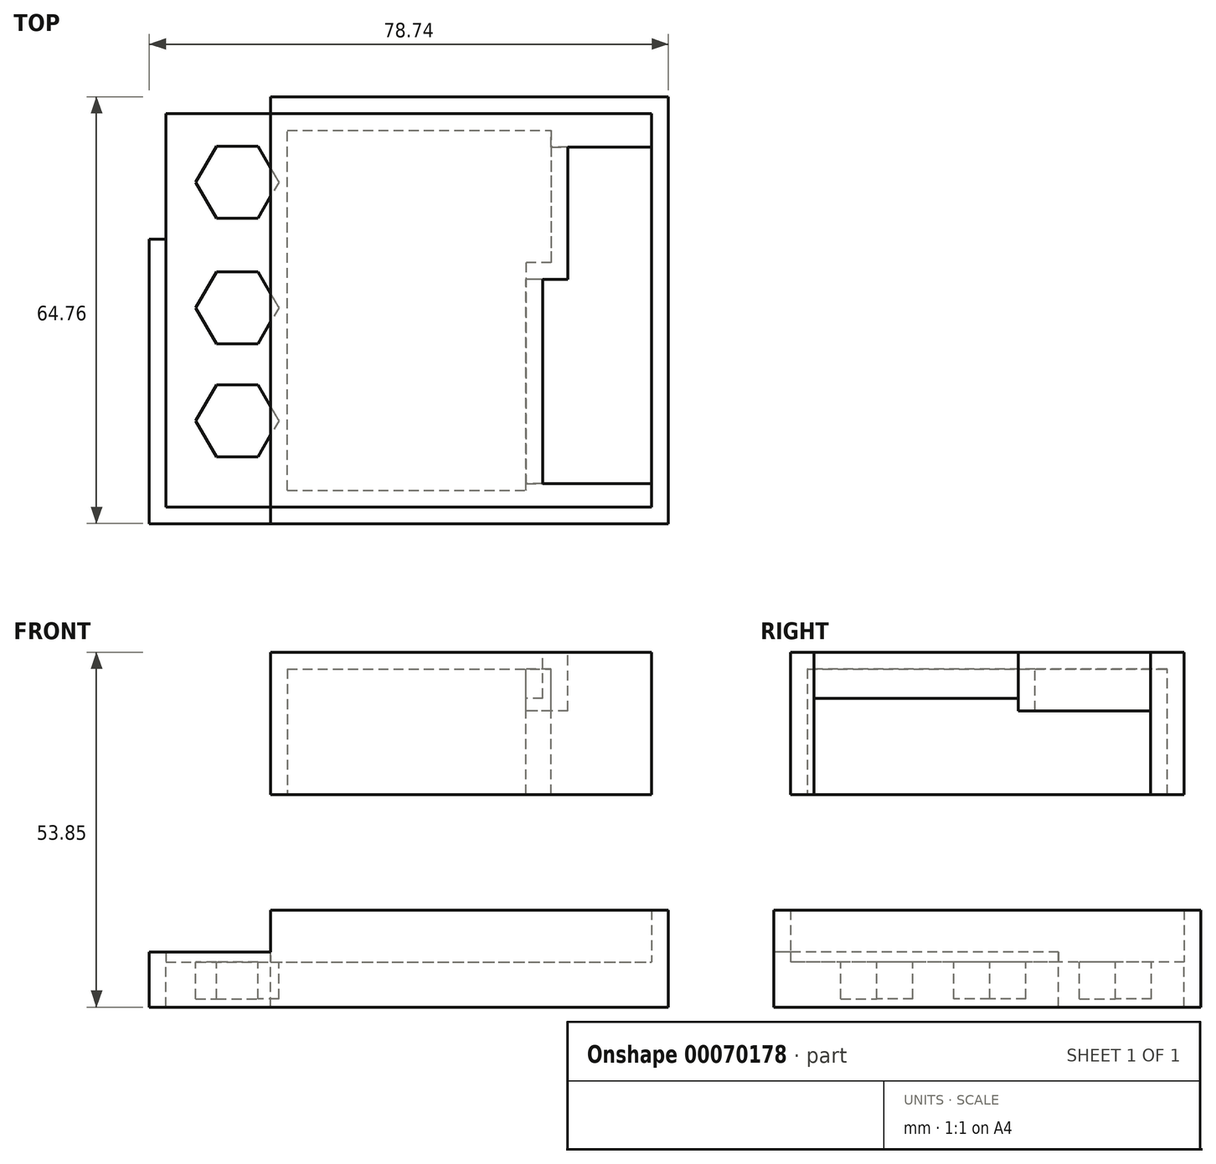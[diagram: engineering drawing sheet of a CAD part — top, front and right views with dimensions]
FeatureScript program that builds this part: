
annotation { "Feature Type Name" : "Feature", "Feature Type Description" : "" }
export const myFeature = defineFeature(function(context is Context, id is Id, definition is map)
    precondition{}
    {
        {
            var Q0;
            Q0=qCreatedBy(makeId("Top.planeOp"),FACE);
            var sketch = newSketch(context, id + "F0", { "sketchPlane" : qUnion([Q0])});
            skLineSegment(sketch, "E0.bottom", {"start": v(-35.56, 28.58) * mm, "end": v(35.56, 28.58) * mm, "construction": true});
            skLineSegment(sketch, "E0.top", {"start": v(-35.56, -28.58) * mm, "end": v(35.56, -28.58) * mm, "construction": true});
            skLineSegment(sketch, "E0.left", {"start": v(-35.56, 28.58) * mm, "end": v(-35.56, -28.58) * mm, "construction": true});
            skLineSegment(sketch, "E0.right", {"start": v(35.56, 28.58) * mm, "end": v(35.56, -28.58) * mm, "construction": true});
            skLineSegment(sketch, "E1", {"start": v(0, 28.58) * mm, "end": v(0, -28.58) * mm, "construction": true});
            skLineSegment(sketch, "E2.0", {"start": v(-36.83, 29.84) * mm, "end": v(36.83, 29.84) * mm});
            skLineSegment(sketch, "E2.1", {"start": v(-36.83, 29.84) * mm, "end": v(-36.83, -29.84) * mm});
            skLineSegment(sketch, "E2.2", {"start": v(-36.83, -29.84) * mm, "end": v(36.83, -29.84) * mm});
            skLineSegment(sketch, "E2.3", {"start": v(36.83, 29.84) * mm, "end": v(36.83, -29.84) * mm});
            skLineSegment(sketch, "E3.0", {"start": v(-39.37, 32.38) * mm, "end": v(39.37, 32.38) * mm});
            skLineSegment(sketch, "E3.1", {"start": v(-39.37, 32.39) * mm, "end": v(-39.37, -32.39) * mm});
            skLineSegment(sketch, "E3.2", {"start": v(-39.37, -32.38) * mm, "end": v(39.37, -32.38) * mm});
            skLineSegment(sketch, "E3.3", {"start": v(39.37, 32.39) * mm, "end": v(39.37, -32.38) * mm});
            skLineSegment(sketch, "E4.bottom", {"start": v(-20.96, 10.8) * mm, "end": v(-39.37, 10.8) * mm});
            skLineSegment(sketch, "E4.top", {"start": v(-20.96, 32.38) * mm, "end": v(-39.37, 32.38) * mm});
            skLineSegment(sketch, "E4.left", {"start": v(-20.96, 10.8) * mm, "end": v(-20.96, 32.38) * mm});
            skLineSegment(sketch, "E4.right", {"start": v(-39.37, 10.8) * mm, "end": v(-39.37, 32.38) * mm});
            skLineSegment(sketch, "E5.MirrorCS", {"start": v(-20.96, -10.8) * mm, "end": v(-39.37, -10.8) * mm});
            skLineSegment(sketch, "E6.MirrorCS", {"start": v(-20.96, -10.8) * mm, "end": v(-20.96, -32.38) * mm});
            skLineSegment(sketch, "E7", {"start": v(-20.96, -10.8) * mm, "end": v(-20.96, 10.8) * mm});
            skSolve(sketch);
        }
        {
            var Q0;
            {var subQ4=sQuery(id+"F0.wireOp",EDGE,"E4.top");Q0=makeQuery(id+"F0.imprint","IMPRINT",FACE,{"disambiguationData":[TD([[makeQuery(id+"F0.imprint","IMPRINT",EDGE,{"derivedFrom":subQ4}),1.0]])]});}
            var Q1;
            {var subQ0=sQuery(id+"F0.wireOp",EDGE,"E2.1");var subQ1=sQuery(id+"F0.wireOp",EDGE,"E2.0");var subQ2=makeQuery(id+"F0.imprint","INTERSECT",VERTEX,{"derivedFrom":[subQ1,subQ0]});Q1=makeQuery(id+"F0.imprint","IMPRINT",FACE,{"disambiguationData":[TD([[makeQuery(id+"F0.imprint","IMPRINT",EDGE,{"disambiguationData":[TD([[subQ2,-1.0]])],"derivedFrom":subQ1}),-1.0]])]});}
            var Q2;
            {var subQ0=sQuery(id+"F0.wireOp",EDGE,"E2.3");Q2=makeQuery(id+"F0.imprint","IMPRINT",FACE,{"disambiguationData":[TD([[makeQuery(id+"F0.imprint","IMPRINT",EDGE,{"derivedFrom":subQ0}),-1.0]])]});}
            var Q3;
            {var subQ7=sQuery(id+"F0.wireOp",EDGE,"E2.2");var subQ8=sQuery(id+"F0.wireOp",EDGE,"E2.1");var subQ9=makeQuery(id+"F0.imprint","INTERSECT",VERTEX,{"derivedFrom":[subQ8,subQ7]});Q3=makeQuery(id+"F0.imprint","IMPRINT",FACE,{"disambiguationData":[TD([[makeQuery(id+"F0.imprint","IMPRINT",EDGE,{"disambiguationData":[TD([[subQ9,1.0]])],"derivedFrom":subQ8}),-1.0]])]});}
            var Q4;
            {var subQ0=sQuery(id+"F0.wireOp",EDGE,"E4.bottom");var subQ1=sQuery(id+"F0.wireOp",EDGE,"E2.1");var subQ2=makeQuery(id+"F0.imprint","INTERSECT",VERTEX,{"derivedFrom":[subQ1,subQ0]});Q4=makeQuery(id+"F0.imprint","IMPRINT",FACE,{"disambiguationData":[TD([[makeQuery(id+"F0.imprint","IMPRINT",EDGE,{"disambiguationData":[TD([[subQ2,-1.0]])],"derivedFrom":subQ1}),-1.0]])]});}
            var Q5;
            {var subQ0=sQuery(id+"F0.wireOp",EDGE,"E2.2");var subQ1=sQuery(id+"F0.wireOp",EDGE,"E2.1");var subQ2=makeQuery(id+"F0.imprint","INTERSECT",VERTEX,{"derivedFrom":[subQ1,subQ0]});Q5=makeQuery(id+"F0.imprint","IMPRINT",FACE,{"disambiguationData":[TD([[makeQuery(id+"F0.imprint","IMPRINT",EDGE,{"disambiguationData":[TD([[subQ2,1.0]])],"derivedFrom":subQ1}),1.0]])]});}
            var Q6;
            {var subQ1=sQuery(id+"F0.wireOp",EDGE,"E2.3");Q6=makeQuery(id+"F0.imprint","IMPRINT",FACE,{"disambiguationData":[TD([[makeQuery(id+"F0.imprint","IMPRINT",EDGE,{"derivedFrom":subQ1}),1.0]])]});}
            var Q7;
            {var subQ5=sQuery(id+"F0.wireOp",EDGE,"E7");Q7=makeQuery(id+"F0.imprint","IMPRINT",FACE,{"disambiguationData":[TD([[makeQuery(id+"F0.imprint","IMPRINT",EDGE,{"derivedFrom":subQ5}),1.0]])]});}
            extrude(context, id + "F1", {"entities" : qUnion([Q0, Q1, Q2, Q3, Q4, Q5, Q6, Q7]), "oppositeDirection" : true, "depth" : 6.86 * mm});
        }
        {
            var Q0;
            {var subQ1=sQuery(id+"F0.wireOp",EDGE,"E2.3");Q0=makeQuery(id+"F0.imprint","IMPRINT",FACE,{"disambiguationData":[TD([[makeQuery(id+"F0.imprint","IMPRINT",EDGE,{"derivedFrom":subQ1}),1.0]])]});}
            var Q1;
            {var subQ7=sQuery(id+"F0.wireOp",EDGE,"E2.2");var subQ8=sQuery(id+"F0.wireOp",EDGE,"E2.1");var subQ9=makeQuery(id+"F0.imprint","INTERSECT",VERTEX,{"derivedFrom":[subQ8,subQ7]});Q1=makeQuery(id+"F0.imprint","IMPRINT",FACE,{"disambiguationData":[TD([[makeQuery(id+"F0.imprint","IMPRINT",EDGE,{"disambiguationData":[TD([[subQ9,1.0]])],"derivedFrom":subQ8}),-1.0]])]});}
            var Q2;
            {var subQ0=sQuery(id+"F0.wireOp",EDGE,"E4.bottom");var subQ1=sQuery(id+"F0.wireOp",EDGE,"E2.1");var subQ2=makeQuery(id+"F0.imprint","INTERSECT",VERTEX,{"derivedFrom":[subQ1,subQ0]});Q2=makeQuery(id+"F0.imprint","IMPRINT",FACE,{"disambiguationData":[TD([[makeQuery(id+"F0.imprint","IMPRINT",EDGE,{"disambiguationData":[TD([[subQ2,-1.0]])],"derivedFrom":subQ1}),-1.0]])]});}
            var Q3;
            {var subQ4=sQuery(id+"F0.wireOp",EDGE,"E4.top");Q3=makeQuery(id+"F0.imprint","IMPRINT",FACE,{"disambiguationData":[TD([[makeQuery(id+"F0.imprint","IMPRINT",EDGE,{"derivedFrom":subQ4}),1.0]])]});}
            extrude(context, id + "F2", {"entities" : qUnion([Q0, Q1, Q2, Q3]), "operationType" : NewBodyOperationType.ADD, "depth" : 1.52 * mm});
        }
        {
            var Q0;
            Q0=makeQuery(id+"F2.opExtrude","CAP_FACE",FACE,{"disambiguationData":[OSD([sQuery(id+"F0.wireOp",EDGE,"E2.0"),sQuery(id+"F0.wireOp",EDGE,"E2.1"),sQuery(id+"F0.wireOp",EDGE,"E2.2"),sQuery(id+"F0.wireOp",EDGE,"E2.3"),sQuery(id+"F0.wireOp",EDGE,"E3.0"),sQuery(id+"F0.wireOp",EDGE,"E3.1"),sQuery(id+"F0.wireOp",EDGE,"E3.2"),sQuery(id+"F0.wireOp",EDGE,"E3.3")])],"isStart":false});
            extrude(context, id + "F3", {"entities" : qUnion([Q0]), "operationType" : NewBodyOperationType.ADD, "depth" : 6.35 * mm});
        }
        {
            var Q0;
            {var subQ4=sQuery(id+"F0.wireOp",EDGE,"E4.top");Q0=makeQuery(id+"F0.imprint","IMPRINT",FACE,{"disambiguationData":[TD([[makeQuery(id+"F0.imprint","IMPRINT",EDGE,{"derivedFrom":subQ4}),1.0]])]});}
            var Q1;
            {var subQ0=sQuery(id+"F0.wireOp",EDGE,"E2.1");var subQ1=sQuery(id+"F0.wireOp",EDGE,"E2.0");var subQ2=makeQuery(id+"F0.imprint","INTERSECT",VERTEX,{"derivedFrom":[subQ1,subQ0]});Q1=makeQuery(id+"F0.imprint","IMPRINT",FACE,{"disambiguationData":[TD([[makeQuery(id+"F0.imprint","IMPRINT",EDGE,{"disambiguationData":[TD([[subQ2,-1.0]])],"derivedFrom":subQ1}),-1.0]])]});}
            var Q2;
            {var subQ0=sQuery(id+"F0.wireOp",EDGE,"E2.2");var subQ1=sQuery(id+"F0.wireOp",EDGE,"E2.1");var subQ2=makeQuery(id+"F0.imprint","INTERSECT",VERTEX,{"derivedFrom":[subQ1,subQ0]});Q2=makeQuery(id+"F0.imprint","IMPRINT",FACE,{"disambiguationData":[TD([[makeQuery(id+"F0.imprint","IMPRINT",EDGE,{"disambiguationData":[TD([[subQ2,1.0]])],"derivedFrom":subQ1}),1.0]])]});}
            var Q3;
            {var subQ7=sQuery(id+"F0.wireOp",EDGE,"E2.2");var subQ8=sQuery(id+"F0.wireOp",EDGE,"E2.1");var subQ9=makeQuery(id+"F0.imprint","INTERSECT",VERTEX,{"derivedFrom":[subQ8,subQ7]});Q3=makeQuery(id+"F0.imprint","IMPRINT",FACE,{"disambiguationData":[TD([[makeQuery(id+"F0.imprint","IMPRINT",EDGE,{"disambiguationData":[TD([[subQ9,1.0]])],"derivedFrom":subQ8}),-1.0]])]});}
            var Q4;
            {var subQ0=sQuery(id+"F0.wireOp",EDGE,"E4.bottom");var subQ1=sQuery(id+"F0.wireOp",EDGE,"E2.1");var subQ2=makeQuery(id+"F0.imprint","INTERSECT",VERTEX,{"derivedFrom":[subQ1,subQ0]});Q4=makeQuery(id+"F0.imprint","IMPRINT",FACE,{"disambiguationData":[TD([[makeQuery(id+"F0.imprint","IMPRINT",EDGE,{"disambiguationData":[TD([[subQ2,-1.0]])],"derivedFrom":subQ1}),-1.0]])]});}
            extrude(context, id + "F4", {"entities" : qUnion([Q0, Q1, Q2, Q3, Q4]), "operationType" : NewBodyOperationType.REMOVE, "depth" : 25.4 * mm, "hasSecondDirection" : true, "secondDirectionOppositeDirection" : false, "secondDirectionDepth" : 1.52 * mm});
        }
        {
            var Q0;
            {var subQ0=sQuery(id+"F0.wireOp",EDGE,"E2.3");Q0=makeQuery(id+"F0.imprint","IMPRINT",FACE,{"disambiguationData":[TD([[makeQuery(id+"F0.imprint","IMPRINT",EDGE,{"derivedFrom":subQ0}),-1.0]])]});}
            extrude(context, id + "F5", {"entities" : qUnion([Q0]), "operationType" : NewBodyOperationType.ADD, "depth" : 47 * mm, "hasSecondDirection" : true, "secondDirectionOppositeDirection" : false, "secondDirectionDepth" : 25.4 * mm});
        }
        {
            var Q0;
            Q0=makeQuery(id+"F5.opExtrude","CAP_FACE",FACE,{"disambiguationData":[OSD([sQuery(id+"F0.wireOp",EDGE,"E2.0"),sQuery(id+"F0.wireOp",EDGE,"E2.2"),sQuery(id+"F0.wireOp",EDGE,"E2.3"),sQuery(id+"F0.wireOp",EDGE,"E4.left"),sQuery(id+"F0.wireOp",EDGE,"E6.MirrorCS"),sQuery(id+"F0.wireOp",EDGE,"E7")])],"isStart":false});
            var sketch = newSketch(context, id + "F6", { "sketchPlane" : qUnion([Q0])});
            skLineSegment(sketch, "E8.bottom", {"start": v(36.83, 24.77) * mm, "end": v(24.13, 24.77) * mm});
            skLineSegment(sketch, "E8.top", {"start": v(36.83, 4.7) * mm, "end": v(24.13, 4.7) * mm});
            skLineSegment(sketch, "E8.left", {"start": v(36.83, 24.77) * mm, "end": v(36.83, 4.7) * mm});
            skLineSegment(sketch, "E8.right", {"start": v(24.13, 24.77) * mm, "end": v(24.13, 4.7) * mm});
            skLineSegment(sketch, "E9.bottom", {"start": v(36.83, 4.7) * mm, "end": v(20.32, 4.7) * mm});
            skLineSegment(sketch, "E9.top", {"start": v(36.83, -26.29) * mm, "end": v(20.32, -26.29) * mm});
            skLineSegment(sketch, "E9.left", {"start": v(36.83, 4.7) * mm, "end": v(36.83, -26.29) * mm});
            skLineSegment(sketch, "E9.right", {"start": v(20.32, 4.7) * mm, "end": v(20.32, -26.29) * mm});
            skSolve(sketch);
        }
        {
            var Q0;
            Q0=makeQuery(id+"F6.imprint","IMPRINT",FACE,{"disambiguationData":[TD([[makeQuery(id+"F6.imprint","IMPRINT",EDGE,{"derivedFrom":sQuery(id+"F6.wireOp",EDGE,"E9.top")}),-1.0]])]});
            var Q1;
            Q1=makeQuery(id+"F6.imprint","IMPRINT",FACE,{"disambiguationData":[TD([[makeQuery(id+"F6.imprint","IMPRINT",EDGE,{"derivedFrom":sQuery(id+"F6.wireOp",EDGE,"E8.bottom")}),1.0]])]});
            extrude(context, id + "F7", {"entities" : qUnion([Q0, Q1]), "operationType" : NewBodyOperationType.REMOVE, "endBound" : BoundingType.UP_TO_NEXT, "oppositeDirection" : true, "depth" : 25.4 * mm});
        }
        {
            var Q0;
            Q0=makeQuery(id+"F5.opExtrude","CAP_FACE",FACE,{"disambiguationData":[OSD([sQuery(id+"F0.wireOp",EDGE,"E2.0"),sQuery(id+"F0.wireOp",EDGE,"E2.2"),sQuery(id+"F0.wireOp",EDGE,"E2.3"),sQuery(id+"F0.wireOp",EDGE,"E4.left"),sQuery(id+"F0.wireOp",EDGE,"E6.MirrorCS"),sQuery(id+"F0.wireOp",EDGE,"E7")])],"isStart":true});
            shell(context, id + "F8", {"entities" : qUnion([Q0]), "thickness" : 2.54 * mm});
        }
        {
            var Q0;
            Q0=qCreatedBy(makeId("Right.planeOp"),FACE);
            var sketch = newSketch(context, id + "F9", { "sketchPlane" : qUnion([Q0])});
            skLineSegment(sketch, "E10.bottom", {"start": v(-26.29, 25.4) * mm, "end": v(24.77, 25.4) * mm});
            skLineSegment(sketch, "E10.top", {"start": v(-26.29, 40) * mm, "end": v(4.7, 40) * mm});
            skLineSegment(sketch, "E10.left", {"start": v(-26.29, 25.4) * mm, "end": v(-26.29, 40) * mm});
            skLineSegment(sketch, "E11", {"start": v(24.77, 25.4) * mm, "end": v(24.77, 38.1) * mm});
            skLineSegment(sketch, "E12", {"start": v(24.77, 38.1) * mm, "end": v(4.7, 38.1) * mm});
            skLineSegment(sketch, "E13", {"start": v(4.7, 38.1) * mm, "end": v(4.7, 40) * mm});
            skSolve(sketch);
        }
        {
            var Q0;
            Q0=makeQuery(id+"F9.imprint","IMPRINT",FACE,{"disambiguationData":[TD([[makeQuery(id+"F9.imprint","IMPRINT",EDGE,{"derivedFrom":sQuery(id+"F9.wireOp",EDGE,"E10.bottom")}),1.0]])]});
            extrude(context, id + "F10", {"entities" : qUnion([Q0]), "operationType" : NewBodyOperationType.REMOVE, "endBound" : BoundingType.THROUGH_ALL, "depth" : 25.4 * mm});
        }
        {
            var Q0;
            {var subQ0=sQuery(id+"F0.wireOp",EDGE,"E2.3");Q0=makeQuery(id+"F0.imprint","IMPRINT",FACE,{"disambiguationData":[TD([[makeQuery(id+"F0.imprint","IMPRINT",EDGE,{"derivedFrom":subQ0}),-1.0]])]});}
            var sketch = newSketch(context, id + "F11", { "sketchPlane" : qUnion([Q0])});
            skLineSegment(sketch, "E14", {"start": v(-26.03, 75.72) * mm, "end": v(-26.04, -77.86) * mm, "construction": true});
            skCircle(sketch, "E15.cCircle", {"center": v(-26.04, 0.38) * mm, "radius": 5.46 * mm, "construction": true});
            skLineSegment(sketch, "E15.0", {"start": v(-29.19, 5.84) * mm, "end": v(-22.88, 5.84) * mm});
            skLineSegment(sketch, "E15.1", {"start": v(-22.88, 5.84) * mm, "end": v(-19.73, 0.38) * mm});
            skLineSegment(sketch, "E15.2", {"start": v(-19.73, 0.38) * mm, "end": v(-22.88, -5.08) * mm});
            skLineSegment(sketch, "E15.3", {"start": v(-22.88, -5.08) * mm, "end": v(-29.19, -5.08) * mm});
            skLineSegment(sketch, "E15.4", {"start": v(-29.19, -5.08) * mm, "end": v(-32.34, 0.38) * mm});
            skLineSegment(sketch, "E15.5", {"start": v(-32.34, 0.38) * mm, "end": v(-29.19, 5.84) * mm});
            skPoint(sketch, "E15.0.midPoint", {"position": v(-26.04, 5.84) * mm});
            skCircle(sketch, "E16.cCircle", {"center": v(-26.04, -16.76) * mm, "radius": 5.46 * mm, "construction": true});
            skLineSegment(sketch, "E16.0", {"start": v(-29.19, -11.3) * mm, "end": v(-22.88, -11.3) * mm});
            skLineSegment(sketch, "E16.1", {"start": v(-22.88, -11.3) * mm, "end": v(-19.73, -16.76) * mm});
            skLineSegment(sketch, "E16.2", {"start": v(-19.73, -16.76) * mm, "end": v(-22.88, -22.23) * mm});
            skLineSegment(sketch, "E16.3", {"start": v(-22.88, -22.23) * mm, "end": v(-29.19, -22.23) * mm});
            skLineSegment(sketch, "E16.4", {"start": v(-29.19, -22.23) * mm, "end": v(-32.34, -16.76) * mm});
            skLineSegment(sketch, "E16.5", {"start": v(-32.34, -16.76) * mm, "end": v(-29.19, -11.3) * mm});
            skPoint(sketch, "E16.0.midPoint", {"position": v(-26.04, -11.3) * mm});
            skCircle(sketch, "E17.cCircle", {"center": v(-26.04, 19.43) * mm, "radius": 5.46 * mm, "construction": true});
            skLineSegment(sketch, "E17.0", {"start": v(-29.19, 24.9) * mm, "end": v(-22.88, 24.9) * mm});
            skLineSegment(sketch, "E17.1", {"start": v(-22.88, 24.9) * mm, "end": v(-19.73, 19.43) * mm});
            skLineSegment(sketch, "E17.2", {"start": v(-19.73, 19.43) * mm, "end": v(-22.88, 13.97) * mm});
            skLineSegment(sketch, "E17.3", {"start": v(-22.88, 13.97) * mm, "end": v(-29.19, 13.97) * mm});
            skLineSegment(sketch, "E17.4", {"start": v(-29.19, 13.97) * mm, "end": v(-32.34, 19.43) * mm});
            skLineSegment(sketch, "E17.5", {"start": v(-32.34, 19.43) * mm, "end": v(-29.19, 24.9) * mm});
            skPoint(sketch, "E17.0.midPoint", {"position": v(-26.04, 24.9) * mm});
            skSolve(sketch);
        }
        {
            var Q0;
            {var subQ5=sQuery(id+"F11.wireOp",EDGE,"E15.0");Q0=makeQuery(id+"F11.imprint","IMPRINT",FACE,{"disambiguationData":[TD([[makeQuery(id+"F11.imprint","IMPRINT",EDGE,{"derivedFrom":subQ5}),-1.0]])]});}
            var Q1;
            {var subQ6=sQuery(id+"F11.wireOp",EDGE,"E16.0");Q1=makeQuery(id+"F11.imprint","IMPRINT",FACE,{"disambiguationData":[TD([[makeQuery(id+"F11.imprint","IMPRINT",EDGE,{"derivedFrom":subQ6}),-1.0]])]});}
            var Q2;
            {var subQ0=sQuery(id+"F11.wireOp",EDGE,"E15.2");var subQ1=sQuery(id+"F11.wireOp",EDGE,"E15.1");var subQ2=makeQuery(id+"F11.imprint","INTERSECT",VERTEX,{"derivedFrom":[subQ1,subQ0]});Q2=makeQuery(id+"F11.imprint","IMPRINT",FACE,{"disambiguationData":[TD([[makeQuery(id+"F11.imprint","IMPRINT",EDGE,{"disambiguationData":[TD([[subQ2,1.0]])],"derivedFrom":subQ1}),-1.0]])]});}
            var Q3;
            {var subQ0=sQuery(id+"F11.wireOp",EDGE,"E16.2");var subQ1=sQuery(id+"F11.wireOp",EDGE,"E16.1");var subQ2=makeQuery(id+"F11.imprint","INTERSECT",VERTEX,{"derivedFrom":[subQ1,subQ0]});Q3=makeQuery(id+"F11.imprint","IMPRINT",FACE,{"disambiguationData":[TD([[makeQuery(id+"F11.imprint","IMPRINT",EDGE,{"disambiguationData":[TD([[subQ2,1.0]])],"derivedFrom":subQ1}),-1.0]])]});}
            var Q4;
            {var subQ0=sQuery(id+"F11.wireOp",EDGE,"E17.2");var subQ1=sQuery(id+"F11.wireOp",EDGE,"E17.1");var subQ2=makeQuery(id+"F11.imprint","INTERSECT",VERTEX,{"derivedFrom":[subQ1,subQ0]});Q4=makeQuery(id+"F11.imprint","IMPRINT",FACE,{"disambiguationData":[TD([[makeQuery(id+"F11.imprint","IMPRINT",EDGE,{"disambiguationData":[TD([[subQ2,1.0]])],"derivedFrom":subQ1}),-1.0]])]});}
            var Q5;
            {var subQ6=sQuery(id+"F11.wireOp",EDGE,"E17.0");Q5=makeQuery(id+"F11.imprint","IMPRINT",FACE,{"disambiguationData":[TD([[makeQuery(id+"F11.imprint","IMPRINT",EDGE,{"derivedFrom":subQ6}),-1.0]])]});}
            extrude(context, id + "F12", {"entities" : qUnion([Q0, Q1, Q2, Q3, Q4, Q5]), "operationType" : NewBodyOperationType.REMOVE, "oppositeDirection" : true, "depth" : 5.6 * mm});
        }
    });
